# Revit family: Layout-Teknion-Emote_06-R2016
name_source: partatom
category: Furniture Systems
revit_build: Autodesk Revit Architecture 2016 (Build: 20190507_1515(x64)
units: mm (PartAtom-declared; Revit-internal decimal feet)

## family parameters
Always vertical = Yes
Cut with Voids When Loaded = No
OmniClass Number = 23.40.70.14.64.21
OmniClass Title = Systems Furniture
Part Type = Normal
Room Calculation Point = No
Round Connector Dimension = Use Diameter
Shared = Yes
Work Plane-Based = No

## types (1)
- Emote 06
    Assembly Code = E2020200
    Description = 5'-0" x 10'-8" Overall
    Manufacturer = Teknion
    Manufacturer Fax = 416.661.4586
    Model = Emote 06 Layout
    Product Line = Emote
    Product Page URL = https://www.teknionplanningtool.com
    Series = Emote
    Sustainability Data = https://www.teknion.com
    URL = www.teknion.com
    Unit Weight URL = http://www.teknion.com
    Warranty = http://www.teknion.com

## geometry (parser evidence)
native form markers: Blend x63, Sweep x16
no freeform markers — native parametric forms only
